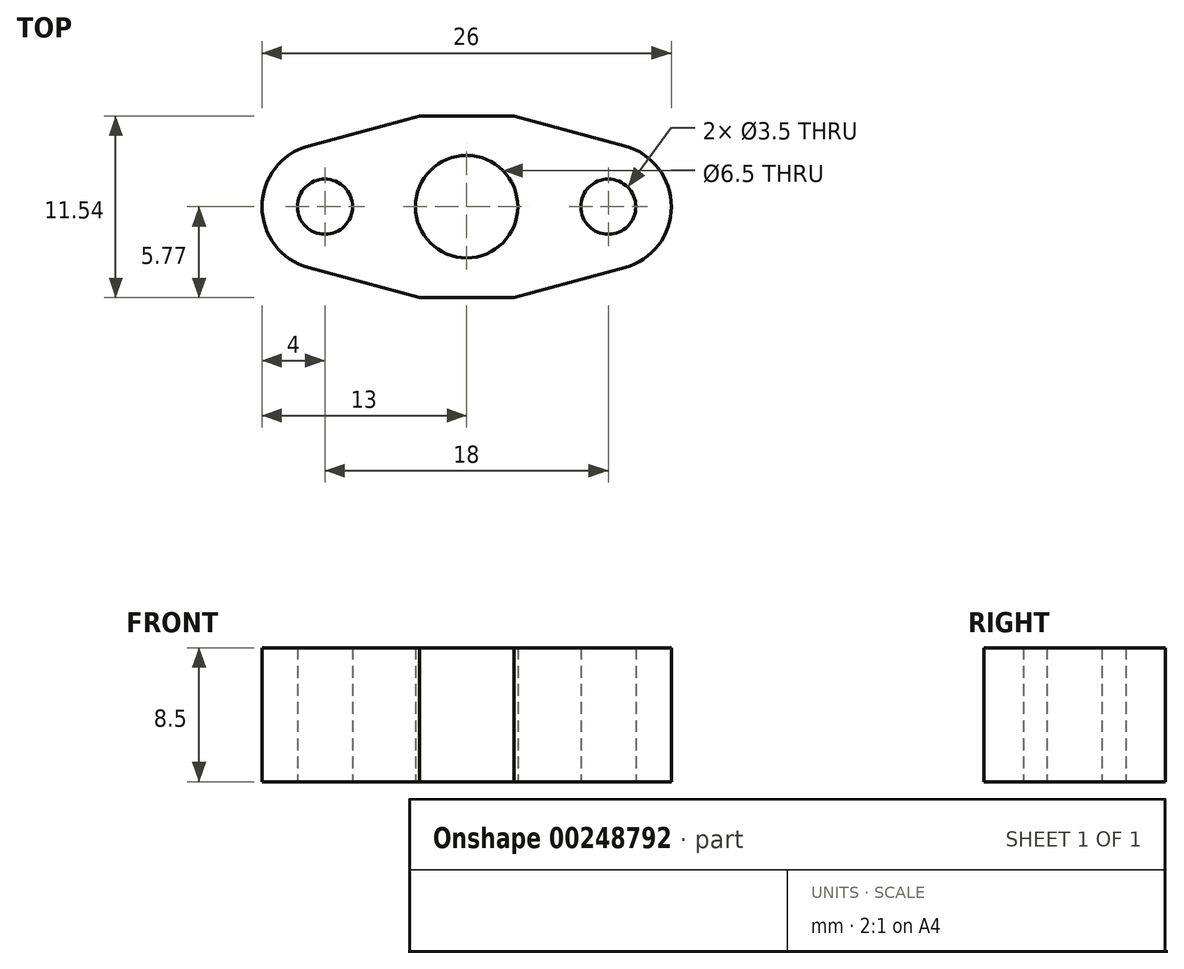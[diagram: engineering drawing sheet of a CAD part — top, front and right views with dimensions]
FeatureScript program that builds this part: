
annotation { "Feature Type Name" : "Feature", "Feature Type Description" : "" }
export const myFeature = defineFeature(function(context is Context, id is Id, definition is map)
    precondition{}
    {
        {
            assignVariable(context, id + "F0", {"variableType" : VariableType.LENGTH, "name" : "h", "lengthValue" : 8.5 * mm});
        }
        {
            var Q0;
            Q0=qCreatedBy(makeId("Top.planeOp"),FACE);
            var sketch = newSketch(context, id + "F1", { "sketchPlane" : qUnion([Q0])});
            skArc(sketch, "E0", {"start": v(-10.04, 3.86) * mm, "mid": v(-13, 0) * mm, "end": v(-10.04, -3.86) * mm});
            skPoint(sketch, "E1", {"position": v(-3, 5.76) * mm});
            skLineSegment(sketch, "E2", {"start": v(-3, 5.77) * mm, "end": v(-10.04, 3.86) * mm});
            skCircle(sketch, "E3", {"center": v(-9, 0) * mm, "radius": 1.75 * mm});
            skLineSegment(sketch, "E4.MirrorCS", {"start": v(3, 5.77) * mm, "end": v(10.04, 3.86) * mm});
            skArc(sketch, "E5.MirrorC", {"start": v(10.04, 3.86) * mm, "mid": v(13, 0) * mm, "end": v(10.04, -3.86) * mm});
            skCircle(sketch, "E6.MirrorC", {"center": v(9, 0) * mm, "radius": 1.75 * mm});
            skLineSegment(sketch, "E7.MirrorCS", {"start": v(-3, -5.77) * mm, "end": v(-10.04, -3.86) * mm});
            skLineSegment(sketch, "E8.MirrorCS", {"start": v(3, -5.77) * mm, "end": v(10.04, -3.86) * mm});
            skLineSegment(sketch, "E9", {"start": v(3, 5.77) * mm, "end": v(-3, 5.77) * mm});
            skLineSegment(sketch, "E10", {"start": v(-3, -5.77) * mm, "end": v(3, -5.77) * mm});
            skCircle(sketch, "E11", {"center": v(0, 0) * mm, "radius": 3.25 * mm});
            skSolve(sketch);
        }
        {
            var Q0;
            Q0=makeQuery(id+"F1.imprint","IMPRINT",FACE,{"disambiguationData":[TD([[makeQuery(id+"F1.imprint","IMPRINT",EDGE,{"derivedFrom":sQuery(id+"F1.wireOp",EDGE,"E0")}),1.0]])]});
            extrude(context, id + "F2", {"entities" : qUnion([Q0]), "depth" : getVariable(context, 'h'), "offsetDistance" : 25 * mm, "symmetric" : true});
        }
    });
